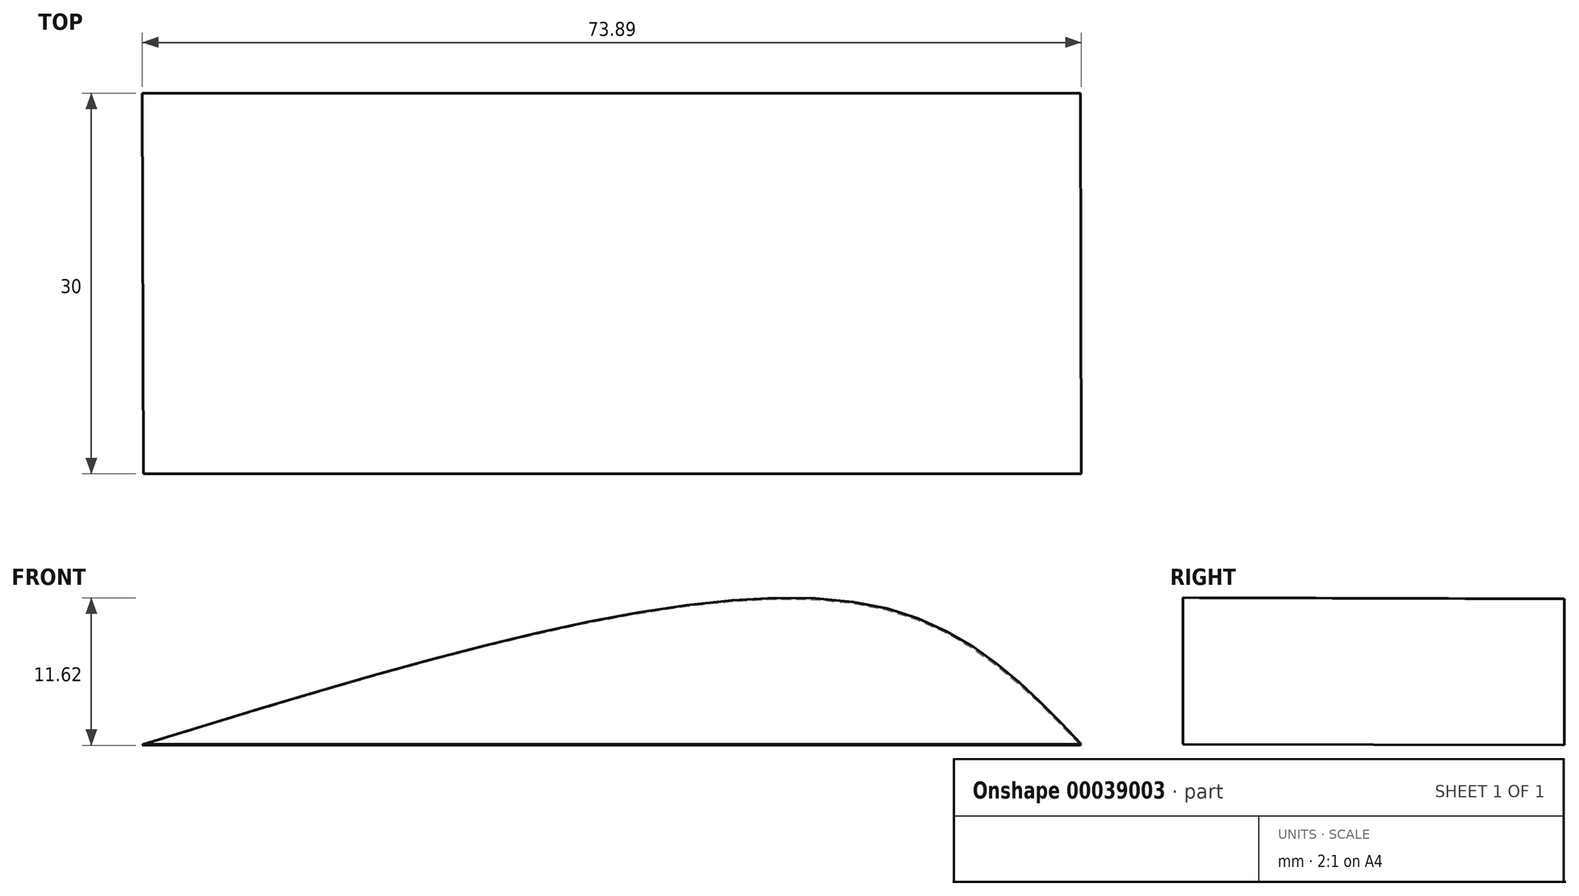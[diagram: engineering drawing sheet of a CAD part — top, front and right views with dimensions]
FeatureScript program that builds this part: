
annotation { "Feature Type Name" : "Feature", "Feature Type Description" : "" }
export const myFeature = defineFeature(function(context is Context, id is Id, definition is map)
    precondition{}
    {
        {
            var Q0;
            Q0=qCreatedBy(makeId("Front.planeOp"),FACE);
            var sketch = newSketch(context, id + "F0", { "sketchPlane" : qUnion([Q0])});
            skLineSegment(sketch, "E0", {"start": v(-30.6, -7.86) * mm, "end": v(43.2, -7.86) * mm});
            skFitSpline(sketch, "E1", {"points": [v(-30.6, -7.86) * mm, v(26.67, 3.1) * mm, v(43.2, -7.86) * mm], "startDerivative": vector(105.13, 32.22) * mm, "endDerivative": vector(36.46, -38.42) * mm});
            skSolve(sketch);
        }
        {
            var Q0;
            Q0=qCreatedBy(makeId("Front.planeOp"),FACE);
            cPlane(context, id + "F1", {"entities" : qUnion([Q0]), "cplaneType" : CPlaneType.OFFSET, "offset" : 30 * mm, "oppositeDirection" : true, "width" : 152.4 * mm, "height" : 152.4 * mm});
        }
        {
            var Q0;
            Q0=qCreatedBy(id+"F1.planeOp",FACE);
            var sketch = newSketch(context, id + "F2", { "sketchPlane" : qUnion([Q0])});
            skLineSegment(sketch, "E2", {"start": v(-30.68, -7.95) * mm, "end": v(43.12, -7.95) * mm});
            skFitSpline(sketch, "E3", {"points": [v(-30.68, -7.95) * mm, v(26.58, 3.01) * mm, v(43.12, -7.95) * mm], "startDerivative": vector(105.13, 32.22) * mm, "endDerivative": vector(36.46, -38.42) * mm});
            skLineSegment(sketch, "E4.0", {"start": v(-10.36, -4.99) * mm, "end": v(35.92, -4.99) * mm});
            skFitSpline(sketch, "E4.1", {"points": [v(-29.82, -10.78) * mm, v(-25.44, -9.43) * mm, v(-16.7, -6.75) * mm, v(-4.08, -3.2) * mm, v(5.66, -0.97) * mm, v(12.72, 0.16) * mm, v(17.6, 0.62) * mm, v(21.24, 0.65) * mm, v(23.86, 0.46) * mm, v(25.67, 0.2) * mm, v(27.32, -0.18) * mm, v(29.36, -0.82) * mm, v(31.66, -1.87) * mm, v(34.15, -3.5) * mm, v(37.26, -6.07) * mm, v(39.46, -8.38) * mm, v(40.98, -9.98) * mm]});
            skSolve(sketch);
        }
        {
            var Q0;
            Q0 = qSketchRegion(id + "F0", true);
            var Q1;
            Q1 = qSketchRegion(id + "F2", true);
            loft(context, id + "F3", {"sheetProfilesArray" : [{ "sheetProfileEntities" : qUnion([Q0]) }, { "sheetProfileEntities" : qUnion([Q1]) }]});
        }
    });
